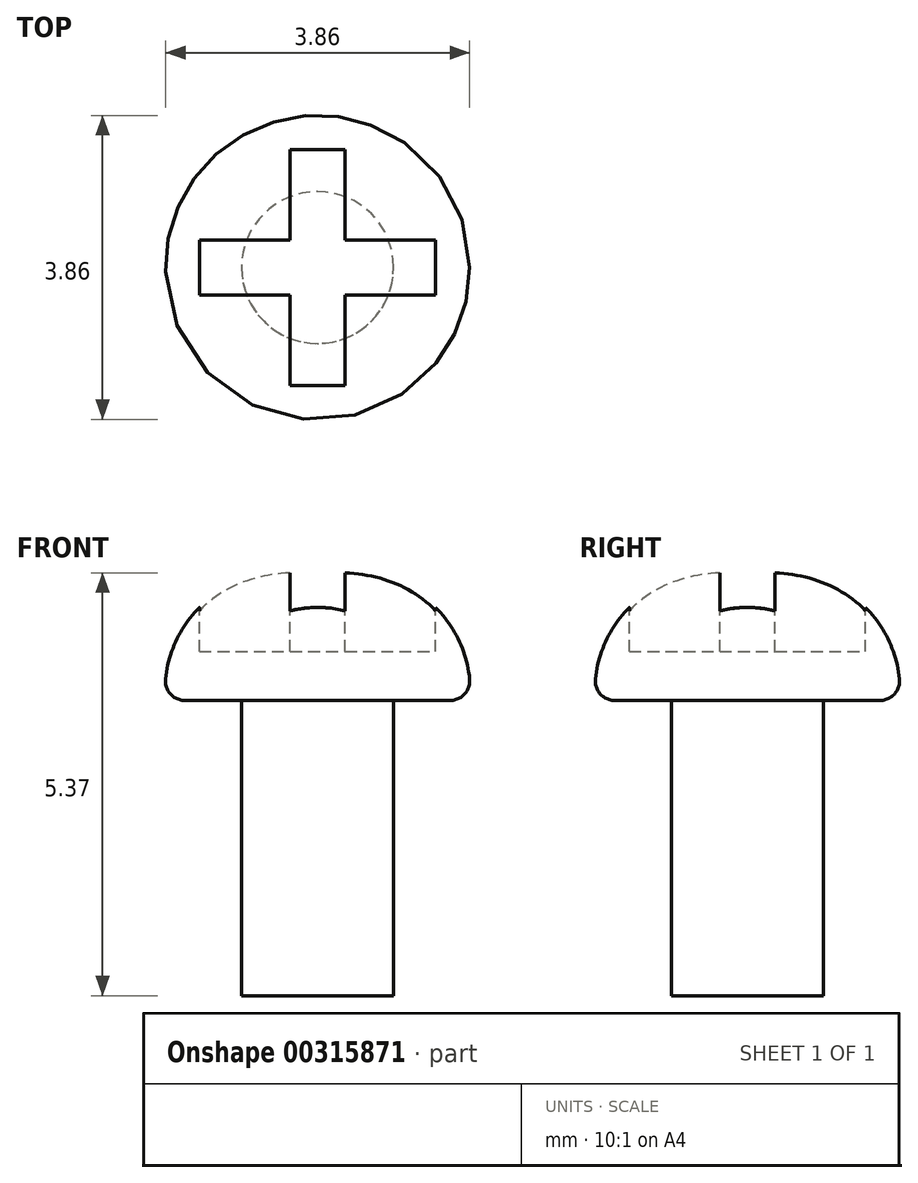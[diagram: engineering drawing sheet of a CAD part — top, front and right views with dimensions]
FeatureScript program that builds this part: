
annotation { "Feature Type Name" : "Feature", "Feature Type Description" : "" }
export const myFeature = defineFeature(function(context is Context, id is Id, definition is map)
    precondition{}
    {
        {
            var Q0;
            Q0=qCreatedBy(makeId("Top.planeOp"),FACE);
            var sketch = newSketch(context, id + "F0", { "sketchPlane" : qUnion([Q0])});
            skCircle(sketch, "E0", {"center": v(0, 0) * mm, "radius": 1.94 * mm});
            skSolve(sketch);
        }
        {
            var Q0;
            Q0=qSketchRegion(id+"F0",true);
            extrude(context, id + "F1", {"entities" : qUnion([Q0]), "depth" : 1.62 * mm});
        }
        {
            var Q0;
            Q0=makeQuery(id+"F1.opExtrude","CAP_FACE",FACE,{"disambiguationData":[OSD([sQuery(id+"F0.wireOp",EDGE,"E0")])],"isStart":false});
            var sketch = newSketch(context, id + "F2", { "sketchPlane" : qUnion([Q0])});
            skLineSegment(sketch, "E1.bottom", {"start": v(-0.35, -1.5) * mm, "end": v(0.35, -1.5) * mm});
            skLineSegment(sketch, "E1.top", {"start": v(-0.35, 1.5) * mm, "end": v(0.35, 1.5) * mm});
            skLineSegment(sketch, "E1.left", {"start": v(-0.35, -1.5) * mm, "end": v(-0.35, 1.5) * mm});
            skLineSegment(sketch, "E1.right", {"start": v(0.35, -1.5) * mm, "end": v(0.35, 1.5) * mm});
            skLineSegment(sketch, "E2.bottom", {"start": v(-1.5, -0.35) * mm, "end": v(1.5, -0.35) * mm});
            skLineSegment(sketch, "E2.top", {"start": v(-1.5, 0.35) * mm, "end": v(1.5, 0.35) * mm});
            skLineSegment(sketch, "E2.left", {"start": v(-1.5, -0.35) * mm, "end": v(-1.5, 0.35) * mm});
            skLineSegment(sketch, "E2.right", {"start": v(1.5, -0.35) * mm, "end": v(1.5, 0.35) * mm});
            skSolve(sketch);
        }
        {
            var Q0;
            Q0=qSketchRegion(id+"F2",true);
            extrude(context, id + "F3", {"entities" : qUnion([Q0]), "operationType" : NewBodyOperationType.REMOVE, "oppositeDirection" : true, "depth" : 1 * mm});
        }
        {
            var Q0;
            Q0=makeQuery(id+"F1.opExtrude","CAP_EDGE",EDGE,{"disambiguationData":[OSD([sQuery(id+"F0.wireOp",EDGE,"E0")])],"isStart":false});
            fillet(context, id + "F4", {"entities" : qUnion([Q0]), "radius" : 1.5 * mm, "tangentPropagation" : true, "allowEdgeOverflow" : false});
        }
        {
            var Q0;
            Q0=makeQuery(id+"F1.opExtrude","CAP_EDGE",EDGE,{"disambiguationData":[OSD([sQuery(id+"F0.wireOp",EDGE,"E0")])],"isStart":true});
            fillet(context, id + "F5", {"entities" : qUnion([Q0]), "radius" : .25 * mm, "tangentPropagation" : true, "allowEdgeOverflow" : false});
        }
        {
            var Q0;
            Q0=makeQuery(id+"F1.opExtrude","CAP_FACE",FACE,{"disambiguationData":[OSD([sQuery(id+"F0.wireOp",EDGE,"E0")])],"isStart":true});
            var sketch = newSketch(context, id + "F6", { "sketchPlane" : qUnion([Q0])});
            skCircle(sketch, "E3", {"center": v(0, 0) * mm, "radius": 0.97 * mm});
            skSolve(sketch);
        }
        {
            var Q0;
            Q0=makeQuery(id+"F6.imprint","IMPRINT",FACE,{"disambiguationData":[TD([[makeQuery(id+"F6.imprint","IMPRINT",EDGE,{"derivedFrom":sQuery(id+"F6.wireOp",EDGE,"E3")}),1.0]])]});
            extrude(context, id + "F7", {"entities" : qUnion([Q0]), "operationType" : NewBodyOperationType.ADD, "depth" : 3.75 * mm});
        }
    });
